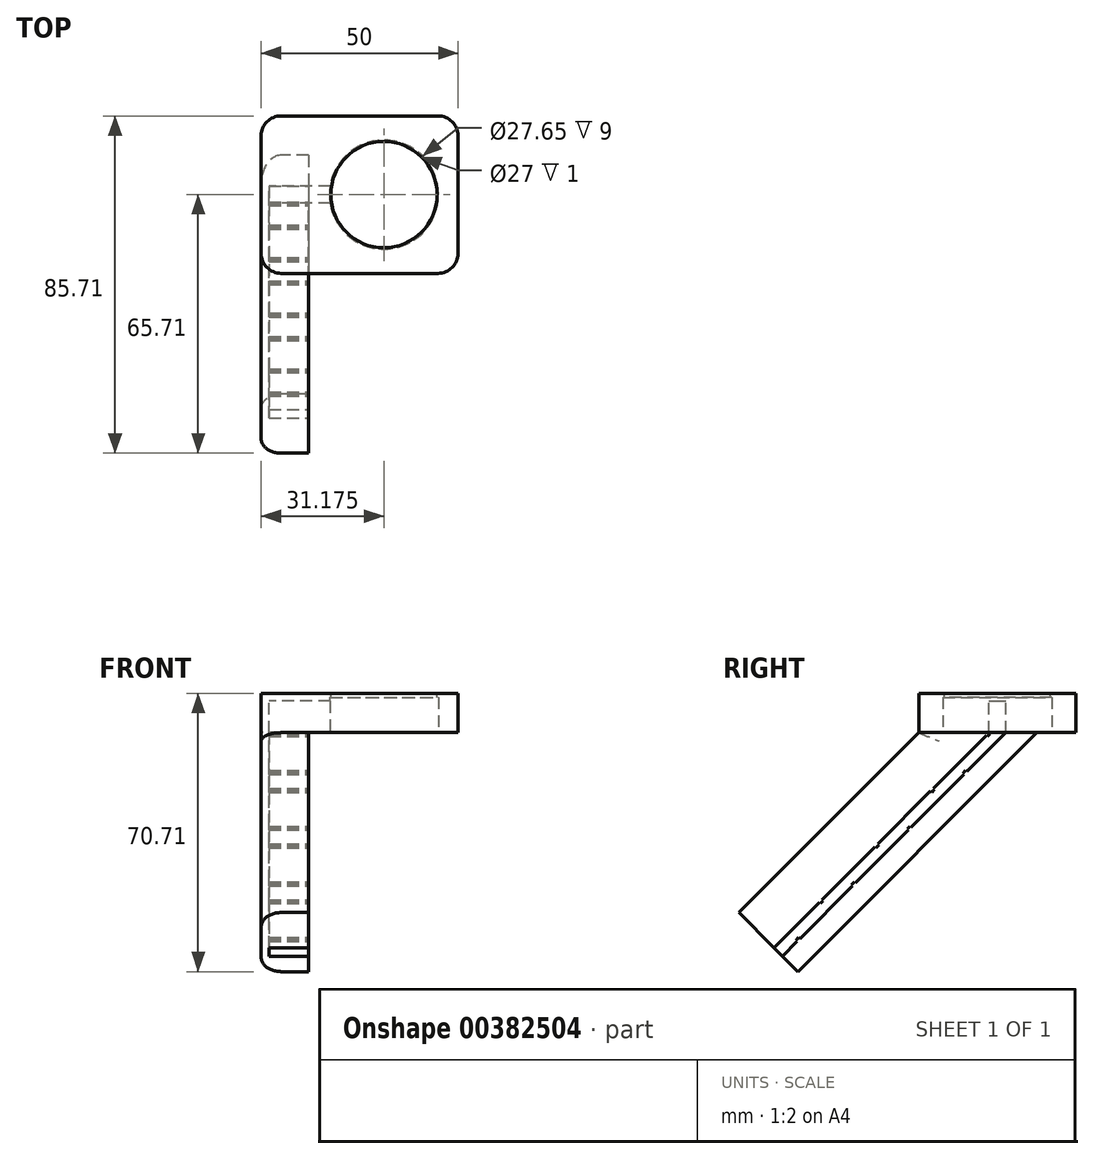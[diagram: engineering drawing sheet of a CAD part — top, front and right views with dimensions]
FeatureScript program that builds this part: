
annotation { "Feature Type Name" : "Feature", "Feature Type Description" : "" }
export const myFeature = defineFeature(function(context is Context, id is Id, definition is map)
    precondition{}
    {
        {
            var Q0;
            Q0=qCreatedBy(makeId("Top.planeOp"),FACE);
            var sketch = newSketch(context, id + "F0", { "sketchPlane" : qUnion([Q0])});
            skLineSegment(sketch, "E0.bottom", {"start": v(25, 20) * mm, "end": v(-25, 20) * mm});
            skLineSegment(sketch, "E0.top", {"start": v(25, -20) * mm, "end": v(-25, -20) * mm});
            skLineSegment(sketch, "E0.left", {"start": v(25, 20) * mm, "end": v(25, -20) * mm});
            skLineSegment(sketch, "E0.right", {"start": v(-25, 20) * mm, "end": v(-25, -20) * mm});
            skPoint(sketch, "E0.middle", {"position": v(0, 0) * mm});
            skSolve(sketch);
        }
        {
            var Q0;
            Q0 = qSketchRegion(id + "F0", true);
            extrude(context, id + "F1", {"entities" : qUnion([Q0]), "depth" : 10 * mm});
        }
        {
            var Q0;
            Q0=makeQuery(id+"F1.opExtrude","CAP_FACE",FACE,{"disambiguationData":[OSD([sQuery(id+"F0.wireOp",EDGE,"E0.bottom"),sQuery(id+"F0.wireOp",EDGE,"E0.top"),sQuery(id+"F0.wireOp",EDGE,"E0.left"),sQuery(id+"F0.wireOp",EDGE,"E0.right")])],"isStart":true});
            var sketch = newSketch(context, id + "F2", { "sketchPlane" : qUnion([Q0])});
            skCircle(sketch, "E1", {"center": v(6.18, 0) * mm, "radius": 13.82 * mm});
            skSolve(sketch);
        }
        {
            var Q0;
            Q0 = qSketchRegion(id + "F2", true);
            extrude(context, id + "F3", {"entities" : qUnion([Q0]), "operationType" : NewBodyOperationType.REMOVE, "oppositeDirection" : true, "depth" : 9 * mm});
        }
        {
            var Q0;
            Q0=makeQuery(id+"F1.opExtrude","CAP_FACE",FACE,{"disambiguationData":[OSD([sQuery(id+"F0.wireOp",EDGE,"E0.bottom"),sQuery(id+"F0.wireOp",EDGE,"E0.top"),sQuery(id+"F0.wireOp",EDGE,"E0.left"),sQuery(id+"F0.wireOp",EDGE,"E0.right")])],"isStart":false});
            var sketch = newSketch(context, id + "F4", { "sketchPlane" : qUnion([Q0])});
            skCircle(sketch, "E2", {"center": v(6.18, 0) * mm, "radius": 13.5 * mm});
            skSolve(sketch);
        }
        {
            var Q0;
            Q0 = qSketchRegion(id + "F4", true);
            extrude(context, id + "F5", {"entities" : qUnion([Q0]), "operationType" : NewBodyOperationType.REMOVE, "endBound" : BoundingType.UP_TO_NEXT, "oppositeDirection" : true, "depth" : 25.4 * mm});
        }
        {
            var Q0;
            Q0=makeQuery(id+"F1.opExtrude","SWEPT_FACE",FACE,{"disambiguationData":[OSD([sQuery(id+"F0.wireOp",EDGE,"E0.right")])]});
            var sketch = newSketch(context, id + "F6", { "sketchPlane" : qUnion([Q0])});
            skLineSegment(sketch, "E3.bottom", {"start": v(-2.13, 8) * mm, "end": v(2.12, 8) * mm});
            skLineSegment(sketch, "E3.top", {"start": v(-2.13, 0) * mm, "end": v(2.12, 0) * mm});
            skLineSegment(sketch, "E3.left", {"start": v(-2.13, 8) * mm, "end": v(-2.13, 0) * mm});
            skLineSegment(sketch, "E3.right", {"start": v(2.12, 8) * mm, "end": v(2.12, 0) * mm});
            skLineSegment(sketch, "E4", {"start": v(-2.13, 8) * mm, "end": v(-20, 8) * mm});
            skLineSegment(sketch, "E5", {"start": v(2.12, 8) * mm, "end": v(20, 8) * mm});
            skSolve(sketch);
        }
        {
            var Q0;
            Q0 = qSketchRegion(id + "F6", true);
            extrude(context, id + "F7", {"entities" : qUnion([Q0]), "operationType" : NewBodyOperationType.REMOVE, "endBound" : BoundingType.UP_TO_NEXT, "oppositeDirection" : true, "depth" : 25.4 * mm});
        }
        {
            var Q0;
            Q0=makeQuery(id+"F1.opExtrude","SWEPT_FACE",FACE,{"disambiguationData":[OSD([sQuery(id+"F0.wireOp",EDGE,"E0.right")])]});
            var sketch = newSketch(context, id + "F8", { "sketchPlane" : qUnion([Q0])});
            skLineSegment(sketch, "E6", {"start": v(-20, 10) * mm, "end": v(50.71, -60.71) * mm});
            skLineSegment(sketch, "E7", {"start": v(50.71, -60.71) * mm, "end": v(65.71, -45.71) * mm});
            skLineSegment(sketch, "E8", {"start": v(-20, 10) * mm, "end": v(10, 10) * mm});
            skLineSegment(sketch, "E9", {"start": v(10, 10) * mm, "end": v(65.71, -45.71) * mm});
            skSolve(sketch);
        }
        {
            var Q0;
            Q0 = qSketchRegion(id + "F8", true);
            extrude(context, id + "F9", {"entities" : qUnion([Q0]), "operationType" : NewBodyOperationType.ADD, "oppositeDirection" : true, "depth" : 12 * mm});
        }
        {
            var Q0;
            Q0=makeQuery(id+"F1.opExtrude","SWEPT_EDGE",EDGE,{"disambiguationData":[OSD([sQuery(id+"F0.wireOp",EDGE,"E0.top"),sQuery(id+"F0.wireOp",EDGE,"E0.left")])]});
            var Q1;
            Q1=makeQuery(id+"F1.opExtrude","SWEPT_EDGE",EDGE,{"disambiguationData":[OSD([sQuery(id+"F0.wireOp",EDGE,"E0.top"),sQuery(id+"F0.wireOp",EDGE,"E0.right")])]});
            var Q2;
            Q2=makeQuery(id+"F1.opExtrude","SWEPT_EDGE",EDGE,{"disambiguationData":[OSD([sQuery(id+"F0.wireOp",EDGE,"E0.bottom"),sQuery(id+"F0.wireOp",EDGE,"E0.right")])]});
            var Q3;
            Q3=makeQuery(id+"F1.opExtrude","SWEPT_EDGE",EDGE,{"disambiguationData":[OSD([sQuery(id+"F0.wireOp",EDGE,"E0.bottom"),sQuery(id+"F0.wireOp",EDGE,"E0.left")])]});
            fillet(context, id + "F10", {"entities" : qUnion([Q0, Q1, Q2, Q3]), "radius" : 5.08 * mm, "tangentPropagation" : true, "allowEdgeOverflow" : false});
        }
        {
            var Q0;
            Q0=makeQuery(id+"F9.opExtrude","CAP_EDGE",EDGE,{"disambiguationData":[OSD([sQuery(id+"F8.wireOp",EDGE,"E9")])],"isStart":true});
            var Q1;
            Q1=makeQuery(id+"F9.opExtrude","CAP_EDGE",EDGE,{"disambiguationData":[OSD([sQuery(id+"F8.wireOp",EDGE,"E6")])],"isStart":true});
            fillet(context, id + "F11", {"entities" : qUnion([Q0, Q1]), "radius" : 5.08 * mm, "tangentPropagation" : true, "allowEdgeOverflow" : false});
        }
        {
            var Q0;
            Q0=makeQuery(id+"F9.opExtrude","CAP_FACE",FACE,{"disambiguationData":[OSD([sQuery(id+"F8.wireOp",EDGE,"E6"),sQuery(id+"F8.wireOp",EDGE,"E7"),sQuery(id+"F8.wireOp",EDGE,"E8"),sQuery(id+"F8.wireOp",EDGE,"E9")])],"isStart":false});
            var sketch = newSketch(context, id + "F12", { "sketchPlane" : qUnion([Q0])});
            skLineSegment(sketch, "E10", {"start": v(-2.12, 8) * mm, "end": v(2.13, 8) * mm});
            skLineSegment(sketch, "E11", {"start": v(2.13, 8) * mm, "end": v(2.13, 0) * mm});
            skLineSegment(sketch, "E12", {"start": v(2.13, 0) * mm, "end": v(-54.65, -56.77) * mm});
            skLineSegment(sketch, "E13", {"start": v(-54.65, -56.77) * mm, "end": v(-56.77, -54.65) * mm});
            skLineSegment(sketch, "E14", {"start": v(-56.77, -54.65) * mm, "end": v(-2.12, 0) * mm});
            skLineSegment(sketch, "E15", {"start": v(-2.12, 0) * mm, "end": v(-2.12, 8) * mm});
            skSolve(sketch);
        }
        {
            var Q0;
            Q0 = qSketchRegion(id + "F12", true);
            extrude(context, id + "F13", {"entities" : qUnion([Q0]), "operationType" : NewBodyOperationType.REMOVE, "oppositeDirection" : true, "depth" : 10 * mm});
        }
        {
            var Q0;
            {var subQ0=sQuery(id+"F8.wireOp",EDGE,"E7");var subQ1=sQuery(id+"F0.wireOp",EDGE,"E0.top");var subQ2=sQuery(id+"F8.wireOp",EDGE,"E9");Q0=makeQuery(id+"F13.boolean.opBoolean","SPLIT",FACE,{"disambiguationData":[TD([makeQuery(id+"F1.opExtrude","SWEPT_FACE",FACE,{"disambiguationData":[OSD([subQ1])]})])],"derivedFrom":makeQuery(id+"F9.opExtrude","CAP_FACE",FACE,{"disambiguationData":[OSD([sQuery(id+"F8.wireOp",EDGE,"E6"),subQ0,sQuery(id+"F8.wireOp",EDGE,"E8"),subQ2])],"isStart":false})});}
            var sketch = newSketch(context, id + "F14", { "sketchPlane" : qUnion([Q0])});
            skLineSegment(sketch, "E16", {"start": v(-2.12, 0) * mm, "end": v(-1.84, -0.28) * mm});
            skLineSegment(sketch, "E17", {"start": v(-1.84, -0.28) * mm, "end": v(-2.55, -0.99) * mm});
            skLineSegment(sketch, "E18", {"start": v(-2.55, -0.99) * mm, "end": v(-2.83, -0.7) * mm});
            skLineSegment(sketch, "E19", {"start": v(-2.83, -0.7) * mm, "end": v(-2.12, 0) * mm});
            skLineSegment(sketch, "E20.1.0.0", {"start": v(-16.97, -14.85) * mm, "end": v(-16.27, -14.14) * mm});
            skLineSegment(sketch, "E20.1.0.1", {"start": v(-15.98, -14.42) * mm, "end": v(-16.7, -15.13) * mm});
            skLineSegment(sketch, "E20.1.0.2", {"start": v(-16.7, -15.13) * mm, "end": v(-16.97, -14.85) * mm});
            skLineSegment(sketch, "E20.1.0.3", {"start": v(-16.27, -14.14) * mm, "end": v(-15.98, -14.42) * mm});
            skLineSegment(sketch, "E20.2.0.0", {"start": v(-31.12, -29) * mm, "end": v(-30.4, -28.28) * mm});
            skLineSegment(sketch, "E20.2.0.1", {"start": v(-30.13, -28.57) * mm, "end": v(-30.83, -29.27) * mm});
            skLineSegment(sketch, "E20.2.0.2", {"start": v(-30.83, -29.27) * mm, "end": v(-31.12, -29) * mm});
            skLineSegment(sketch, "E20.2.0.3", {"start": v(-30.4, -28.28) * mm, "end": v(-30.13, -28.57) * mm});
            skLineSegment(sketch, "E20.direction1", {"start": v(-2.55, -0.99) * mm, "end": v(-16.7, -15.13) * mm, "construction": true});
            skLineSegment(sketch, "E21.0.3.0", {"start": v(-45.26, -43.13) * mm, "end": v(-44.55, -42.43) * mm});
            skLineSegment(sketch, "E21.3.3.0", {"start": v(-44.27, -42.7) * mm, "end": v(-44.98, -43.42) * mm});
            skLineSegment(sketch, "E21.6.3.0", {"start": v(-44.98, -43.42) * mm, "end": v(-45.26, -43.13) * mm});
            skLineSegment(sketch, "E21.9.3.0", {"start": v(-44.55, -42.43) * mm, "end": v(-44.27, -42.7) * mm});
            skSolve(sketch);
        }
        {
            var Q0;
            Q0 = qSketchRegion(id + "F14", true);
            extrude(context, id + "F15", {"entities" : qUnion([Q0]), "operationType" : NewBodyOperationType.ADD, "endBound" : BoundingType.UP_TO_NEXT, "oppositeDirection" : true, "depth" : 25 * mm});
        }
        {
            var Q0;
            {var subQ0=sQuery(id+"F8.wireOp",EDGE,"E6");var subQ1=sQuery(id+"F8.wireOp",EDGE,"E7");Q0=makeQuery(id+"F13.boolean.opBoolean","SPLIT",FACE,{"disambiguationData":[TD([makeQuery(id+"F7.boolean.opBoolean","COPY",FACE,{"derivedFrom":makeQuery(id+"F7.opExtrude","SWEPT_FACE",FACE,{"disambiguationData":[OSD([sQuery(id+"F6.wireOp",EDGE,"E3.left")])]})})])],"derivedFrom":makeQuery(id+"F9.opExtrude","CAP_FACE",FACE,{"disambiguationData":[OSD([subQ0,subQ1,sQuery(id+"F8.wireOp",EDGE,"E8"),sQuery(id+"F8.wireOp",EDGE,"E9")])],"isStart":false})});}
            var sketch = newSketch(context, id + "F16", { "sketchPlane" : qUnion([Q0])});
            skLineSegment(sketch, "E22", {"start": v(-7.78, -9.9) * mm, "end": v(-8.06, -9.62) * mm});
            skLineSegment(sketch, "E23", {"start": v(-8.06, -9.62) * mm, "end": v(-8.77, -10.33) * mm});
            skLineSegment(sketch, "E24", {"start": v(-8.77, -10.33) * mm, "end": v(-8.49, -10.61) * mm});
            skLineSegment(sketch, "E25", {"start": v(-8.49, -10.61) * mm, "end": v(-7.78, -9.9) * mm});
            skLineSegment(sketch, "E26.1.0.0", {"start": v(-22.63, -24.75) * mm, "end": v(-21.92, -24.05) * mm});
            skLineSegment(sketch, "E26.1.0.1", {"start": v(-22.91, -24.47) * mm, "end": v(-22.63, -24.75) * mm});
            skLineSegment(sketch, "E26.1.0.2", {"start": v(-22.2, -23.76) * mm, "end": v(-22.91, -24.47) * mm});
            skLineSegment(sketch, "E26.1.0.3", {"start": v(-21.92, -24.05) * mm, "end": v(-22.2, -23.76) * mm});
            skLineSegment(sketch, "E26.2.0.0", {"start": v(-36.77, -38.9) * mm, "end": v(-36.06, -38.19) * mm});
            skLineSegment(sketch, "E26.2.0.1", {"start": v(-37.05, -38.61) * mm, "end": v(-36.77, -38.9) * mm});
            skLineSegment(sketch, "E26.2.0.2", {"start": v(-36.35, -37.9) * mm, "end": v(-37.05, -38.61) * mm});
            skLineSegment(sketch, "E26.2.0.3", {"start": v(-36.06, -38.19) * mm, "end": v(-36.35, -37.9) * mm});
            skLineSegment(sketch, "E26.3.0.0", {"start": v(-50.91, -53.04) * mm, "end": v(-50.2, -52.33) * mm});
            skLineSegment(sketch, "E26.3.0.1", {"start": v(-51.2, -52.75) * mm, "end": v(-50.91, -53.04) * mm});
            skLineSegment(sketch, "E26.3.0.2", {"start": v(-50.49, -52.05) * mm, "end": v(-51.2, -52.75) * mm});
            skLineSegment(sketch, "E26.3.0.3", {"start": v(-50.2, -52.33) * mm, "end": v(-50.49, -52.05) * mm});
            skLineSegment(sketch, "E26.direction1", {"start": v(-8.49, -10.61) * mm, "end": v(-22.63, -24.75) * mm, "construction": true});
            skSolve(sketch);
        }
        {
            var Q0;
            Q0 = qSketchRegion(id + "F16", true);
            extrude(context, id + "F17", {"entities" : qUnion([Q0]), "operationType" : NewBodyOperationType.ADD, "endBound" : BoundingType.UP_TO_NEXT, "oppositeDirection" : true, "depth" : 25 * mm});
        }
    });
